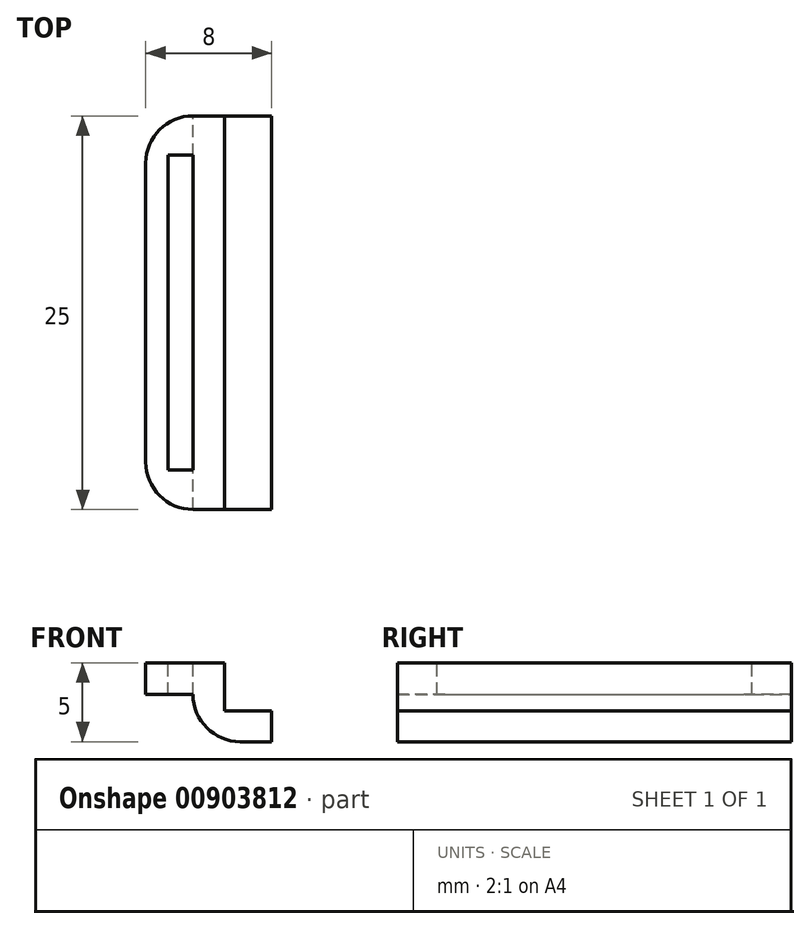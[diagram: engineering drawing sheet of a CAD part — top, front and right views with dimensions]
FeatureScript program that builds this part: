
annotation { "Feature Type Name" : "Feature", "Feature Type Description" : "" }
export const myFeature = defineFeature(function(context is Context, id is Id, definition is map)
    precondition{}
    {
        {
            var Q0;
            Q0=qCreatedBy(makeId("Front.planeOp"),FACE);
            var sketch = newSketch(context, id + "F0", { "sketchPlane" : qUnion([Q0])});
            skLineSegment(sketch, "E0", {"start": v(0, 5) * mm, "end": v(0, 0) * mm});
            skLineSegment(sketch, "E1", {"start": v(0, 0) * mm, "end": v(5, 0) * mm});
            skLineSegment(sketch, "E2", {"start": v(0, 5) * mm, "end": v(2, 5) * mm});
            skLineSegment(sketch, "E3", {"start": v(2, 5) * mm, "end": v(2, 1.96) * mm});
            skLineSegment(sketch, "E4", {"start": v(2, 1.96) * mm, "end": v(5, 1.96) * mm});
            skLineSegment(sketch, "E5", {"start": v(5, 1.96) * mm, "end": v(5, 0) * mm});
            skSolve(sketch);
        }
        {
            var Q0;
            Q0 = qSketchRegion(id + "F0", true);
            extrude(context, id + "F1", {"entities" : qUnion([Q0]), "depth" : 25 * mm, "offsetDistance" : 25 * mm});
        }
        {
            var Q0;
            Q0=makeQuery(id+"F1.opExtrude","SWEPT_EDGE",EDGE,{"disambiguationData":[OSD([sQuery(id+"F0.wireOp",EDGE,"E0"),sQuery(id+"F0.wireOp",EDGE,"E1")])]});
            fillet(context, id + "F2", {"entities" : qUnion([Q0]), "radius" : 3 * mm, "tangentPropagation" : true, "allowEdgeOverflow" : false});
        }
        {
            var Q0;
            Q0=makeQuery(id+"F1.opExtrude","SWEPT_FACE",FACE,{"disambiguationData":[OSD([sQuery(id+"F0.wireOp",EDGE,"E0")])]});
            var sketch = newSketch(context, id + "F3", { "sketchPlane" : qUnion([Q0])});
            skLineSegment(sketch, "E6.bottom", {"start": v(0, 5) * mm, "end": v(25, 5) * mm});
            skLineSegment(sketch, "E6.top", {"start": v(0, 3) * mm, "end": v(25, 3) * mm});
            skLineSegment(sketch, "E6.left", {"start": v(0, 5) * mm, "end": v(0, 3) * mm});
            skLineSegment(sketch, "E6.right", {"start": v(25, 5) * mm, "end": v(25, 3) * mm});
            skSolve(sketch);
        }
        {
            var Q0;
            Q0 = qSketchRegion(id + "F3", true);
            extrude(context, id + "F4", {"entities" : qUnion([Q0]), "operationType" : NewBodyOperationType.ADD, "depth" : 3 * mm, "offsetDistance" : 25 * mm});
        }
        {
            var Q0;
            Q0=makeQuery(id+"F4.boolean.opBoolean","MERGE",FACE,{"derivedFrom":[makeQuery(id+"F1.opExtrude","SWEPT_FACE",FACE,{"disambiguationData":[OSD([sQuery(id+"F0.wireOp",EDGE,"E2")])]}),makeQuery(id+"F4.opExtrude","SWEPT_FACE",FACE,{"disambiguationData":[OSD([sQuery(id+"F3.wireOp",EDGE,"E6.bottom")])]})]});
            var sketch = newSketch(context, id + "F5", { "sketchPlane" : qUnion([Q0])});
            skLineSegment(sketch, "E7.bottom", {"start": v(0, -22.5) * mm, "end": v(-1.6, -22.5) * mm});
            skLineSegment(sketch, "E7.top", {"start": v(0, -2.5) * mm, "end": v(-1.6, -2.5) * mm});
            skLineSegment(sketch, "E7.left", {"start": v(0, -22.5) * mm, "end": v(0, -2.5) * mm});
            skLineSegment(sketch, "E7.right", {"start": v(-1.6, -22.5) * mm, "end": v(-1.6, -2.5) * mm});
            skSolve(sketch);
        }
        {
            var Q0;
            Q0 = qSketchRegion(id + "F5", true);
            extrude(context, id + "F6", {"entities" : qUnion([Q0]), "operationType" : NewBodyOperationType.REMOVE, "endBound" : BoundingType.SYMMETRIC, "oppositeDirection" : true, "depth" : 25 * mm, "offsetDistance" : 25 * mm});
        }
        {
            var Q0;
            Q0=makeQuery(id+"F4.opExtrude","CAP_EDGE",EDGE,{"disambiguationData":[OSD([sQuery(id+"F3.wireOp",EDGE,"E6.left")])],"isStart":false});
            var Q1;
            Q1=makeQuery(id+"F4.opExtrude","CAP_EDGE",EDGE,{"disambiguationData":[OSD([sQuery(id+"F3.wireOp",EDGE,"E6.right")])],"isStart":false});
            fillet(context, id + "F7", {"entities" : qUnion([Q0, Q1]), "radius" : 3 * mm, "tangentPropagation" : true, "allowEdgeOverflow" : false});
        }
    });
